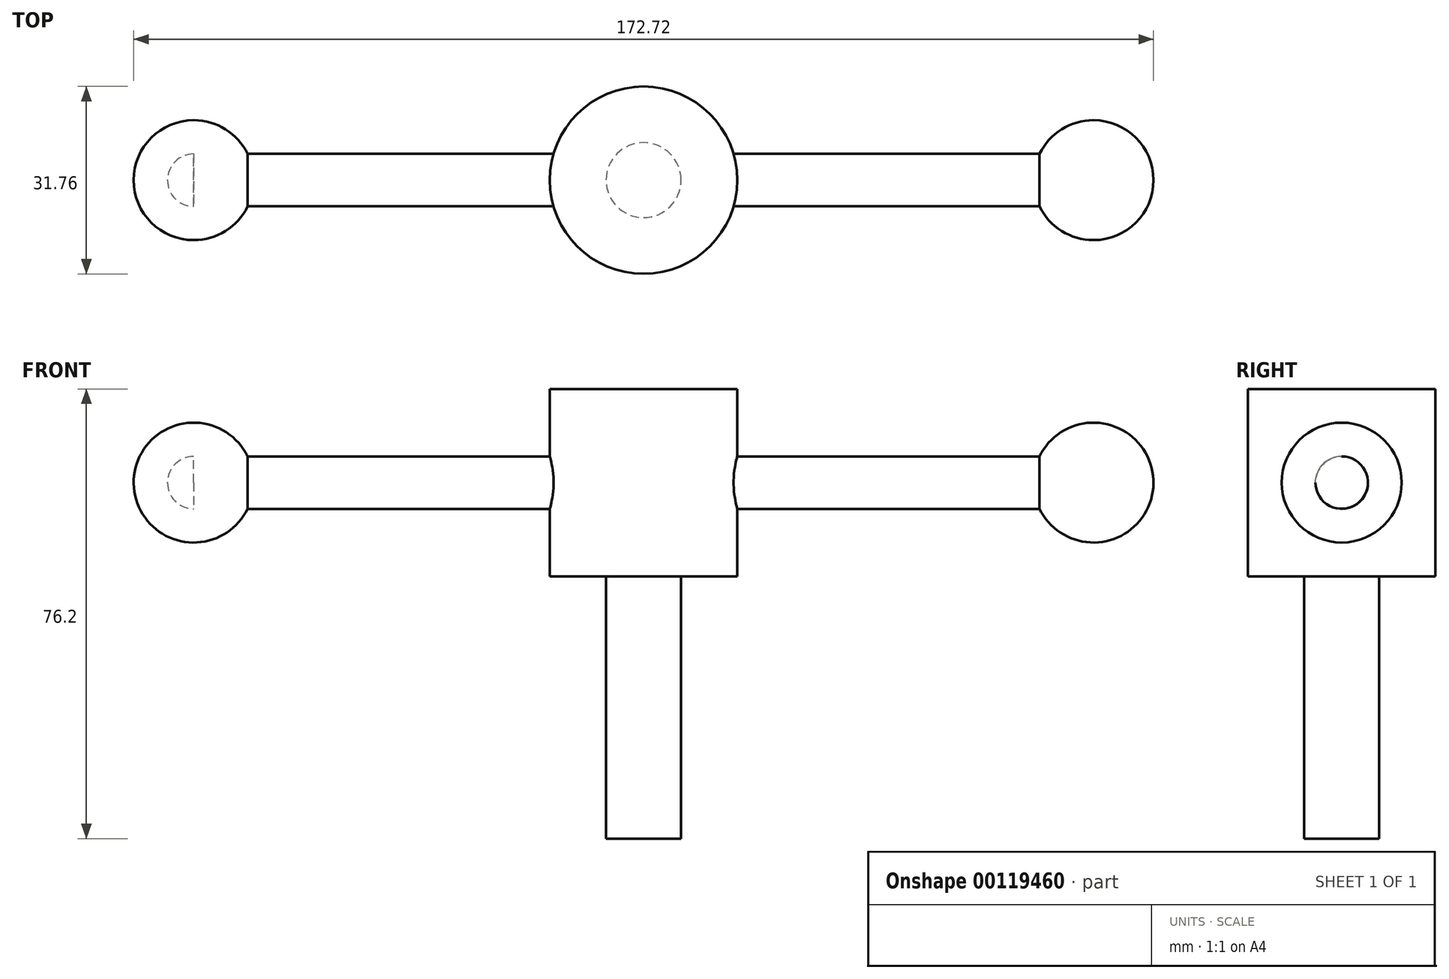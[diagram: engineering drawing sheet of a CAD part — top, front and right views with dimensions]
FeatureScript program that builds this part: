
annotation { "Feature Type Name" : "Feature", "Feature Type Description" : "" }
export const myFeature = defineFeature(function(context is Context, id is Id, definition is map)
    precondition{}
    {
        {
            var Q0;
            Q0=qCreatedBy(makeId("Top.planeOp"),FACE);
            var sketch = newSketch(context, id + "F0", { "sketchPlane" : qUnion([Q0])});
            skCircle(sketch, "E0", {"center": v(0, 0) * mm, "radius": 15.88 * mm});
            skCircle(sketch, "E1", {"center": v(76.2, 0) * mm, "radius": 10.16 * mm});
            skCircle(sketch, "E2", {"center": v(-76.2, 0) * mm, "radius": 10.16 * mm});
            skCircle(sketch, "E3", {"center": v(0, 0) * mm, "radius": 6.35 * mm});
            skSolve(sketch);
        }
        {
            var Q0;
            Q0=makeQuery(id+"F0.imprint","IMPRINT",FACE,{"disambiguationData":[TD([[makeQuery(id+"F0.imprint","IMPRINT",EDGE,{"derivedFrom":sQuery(id+"F0.wireOp",EDGE,"E0")}),1.0]])]});
            var Q1;
            Q1=makeQuery(id+"F0.imprint","IMPRINT",FACE,{"disambiguationData":[TD([[makeQuery(id+"F0.imprint","IMPRINT",EDGE,{"derivedFrom":sQuery(id+"F0.wireOp",EDGE,"E3")}),1.0]])]});
            extrude(context, id + "F1", {"entities" : qUnion([Q0, Q1]), "oppositeDirection" : true, "depth" : 31.75 * mm});
        }
        {
            var Q0;
            Q0=makeQuery(id+"F0.imprint","IMPRINT",FACE,{"disambiguationData":[TD([[makeQuery(id+"F0.imprint","IMPRINT",EDGE,{"derivedFrom":sQuery(id+"F0.wireOp",EDGE,"E3")}),1.0]])]});
            extrude(context, id + "F2", {"entities" : qUnion([Q0]), "operationType" : NewBodyOperationType.ADD, "oppositeDirection" : true, "depth" : 76.2 * mm});
        }
        {
            var Q0;
            Q0=qCreatedBy(makeId("Right.planeOp"),FACE);
            var sketch = newSketch(context, id + "F3", { "sketchPlane" : qUnion([Q0])});
            skCircle(sketch, "E4", {"center": v(0, -15.88) * mm, "radius": 4.45 * mm});
            skSolve(sketch);
        }
        {
            var Q0;
            Q0 = qSketchRegion(id + "F3", true);
            extrude(context, id + "F4", {"entities" : qUnion([Q0]), "operationType" : NewBodyOperationType.ADD, "endBound" : BoundingType.SYMMETRIC, "depth" : 152.4 * mm});
        }
        {
            var Q0;
            Q0=makeQuery(id+"F4.opExtrude","CAP_FACE",FACE,{"disambiguationData":[OSD([sQuery(id+"F3.wireOp",EDGE,"E4")])],"isStart":false});
            var sketch = newSketch(context, id + "F5", { "sketchPlane" : qUnion([Q0])});
            skLineSegment(sketch, "E5", {"start": v(0, -15.88) * mm, "end": v(20.32, -15.88) * mm, "construction": true});
            skLineSegment(sketch, "E6", {"start": v(20.32, -15.88) * mm, "end": v(-15.68, -15.88) * mm, "construction": true});
            skArc(sketch, "E7", {"start": v(10.16, -15.88) * mm, "mid": v(0, -5.71) * mm, "end": v(-10.16, -15.88) * mm});
            skLineSegment(sketch, "E8", {"start": v(-10.16, -15.88) * mm, "end": v(10.16, -15.88) * mm});
            skSolve(sketch);
        }
        {
            var Q0;
            Q0 = qSketchRegion(id + "F5", true);
            var Q1;
            Q1=sQuery(id+"F5.wireOp",EDGE,"E5");
            revolve(context, id + "F6", {"operationType" : NewBodyOperationType.ADD, "entities" : qUnion([Q0]), "axis" : qUnion([Q1]), "revolveType" : RevolveType.FULL});
        }
        {
            var Q0;
            Q0=makeQuery(id+"F4.opExtrude","CAP_FACE",FACE,{"disambiguationData":[OSD([sQuery(id+"F3.wireOp",EDGE,"E4")])],"isStart":true});
            var sketch = newSketch(context, id + "F7", { "sketchPlane" : qUnion([Q0])});
            skLineSegment(sketch, "E9", {"start": v(0, -15.88) * mm, "end": v(20.32, -15.88) * mm, "construction": true});
            skArc(sketch, "E10", {"start": v(10.16, -15.88) * mm, "mid": v(0, -5.71) * mm, "end": v(-10.16, -15.88) * mm});
            skLineSegment(sketch, "E11", {"start": v(-10.16, -15.88) * mm, "end": v(10.16, -15.88) * mm});
            skSolve(sketch);
        }
        {
            var Q0;
            {var subQ0=sQuery(id+"F7.wireOp",EDGE,"E10");Q0=makeQuery(id+"F7.imprint","IMPRINT",FACE,{"disambiguationData":[TD([[makeQuery(id+"F7.imprint","IMPRINT",EDGE,{"derivedFrom":subQ0}),1.0]])]});}
            var Q1;
            Q1=sQuery(id+"F7.wireOp",EDGE,"E9");
            revolve(context, id + "F8", {"operationType" : NewBodyOperationType.ADD, "entities" : qUnion([Q0]), "axis" : qUnion([Q1]), "revolveType" : RevolveType.FULL});
        }
    });
